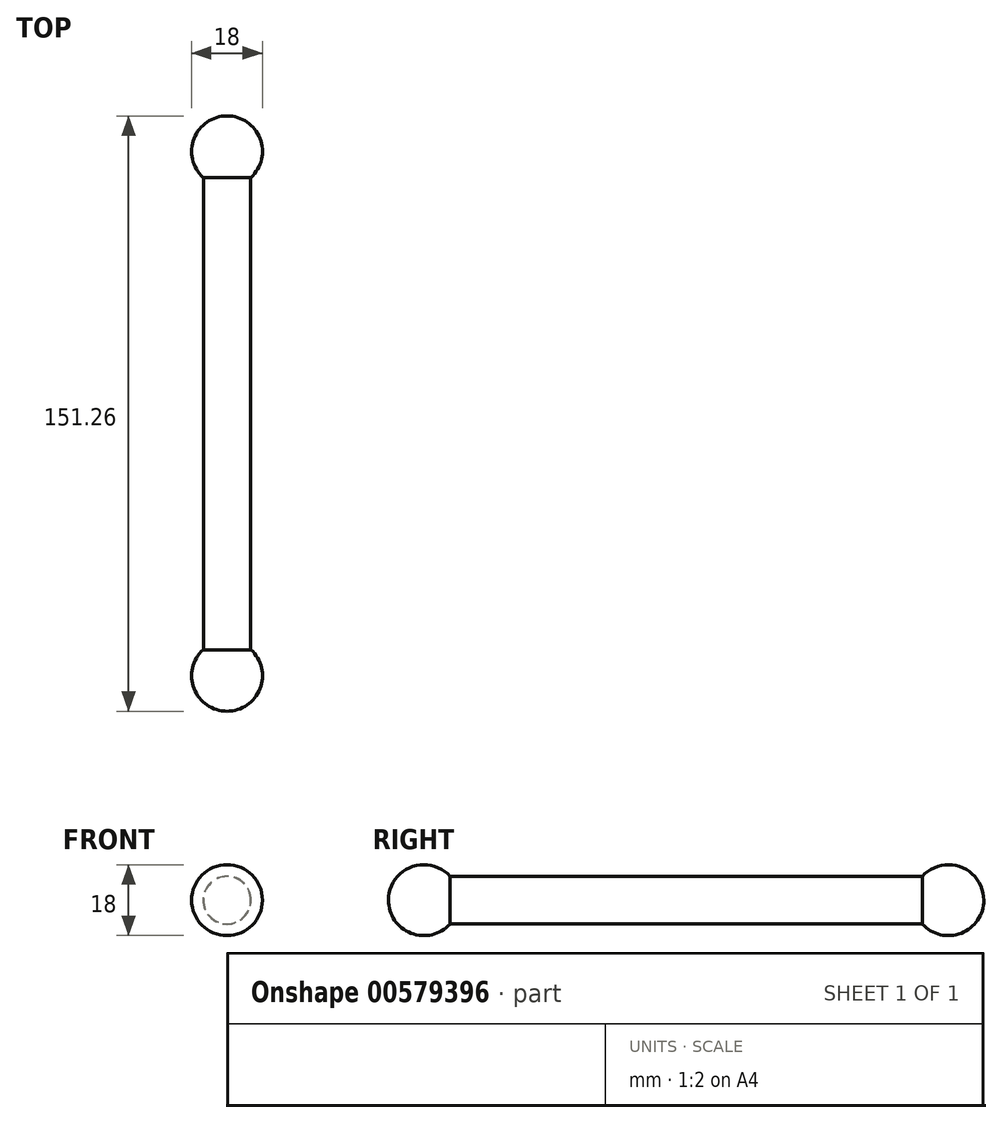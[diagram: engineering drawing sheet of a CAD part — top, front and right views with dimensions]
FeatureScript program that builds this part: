
annotation { "Feature Type Name" : "Feature", "Feature Type Description" : "" }
export const myFeature = defineFeature(function(context is Context, id is Id, definition is map)
    precondition{}
    {
        {
            var Q0;
            Q0=qCreatedBy(makeId("Front.planeOp"),FACE);
            var sketch = newSketch(context, id + "F0", { "sketchPlane" : qUnion([Q0])});
            skCircle(sketch, "E0", {"center": v(0, 0) * mm, "radius": 6 * mm});
            skSolve(sketch);
        }
        {
            var Q0;
            Q0 = qSketchRegion(id + "F0", true);
            extrude(context, id + "F1", {"entities" : qUnion([Q0]), "endBound" : BoundingType.SYMMETRIC, "depth" : 120 * mm, "offsetDistance" : 25 * mm});
        }
        {
            var Q0;
            Q0=qCreatedBy(makeId("Right.planeOp"),FACE);
            var sketch = newSketch(context, id + "F2", { "sketchPlane" : qUnion([Q0])});
            skLineSegment(sketch, "E1", {"start": v(-60, 0) * mm, "end": v(-87.62, 0) * mm, "construction": true});
            skArc(sketch, "E2", {"start": v(-60, 6.1) * mm, "mid": v(-69.9, 8.39) * mm, "end": v(-75.63, 0) * mm});
            skPoint(sketch, "E3", {"position": v(-60, 6.1) * mm});
            skLineSegment(sketch, "E4", {"start": v(-60, 0) * mm, "end": v(-60, 6.1) * mm});
            skLineSegment(sketch, "E5", {"start": v(-60, 0) * mm, "end": v(-75.63, 0) * mm});
            skSolve(sketch);
        }
        {
            var Q0;
            Q0 = qSketchRegion(id + "F2", true);
            var Q1;
            Q1=sQuery(id+"F2.wireOp",EDGE,"E1");
            revolve(context, id + "F3", {"operationType" : NewBodyOperationType.ADD, "entities" : qUnion([Q0]), "axis" : qUnion([Q1]), "revolveType" : RevolveType.FULL});
        }
        {
            var Q0;
            Q0=makeQuery(id+"F1.opExtrude","SWEPT_BODY",BODY,{"disambiguationData":[OSD([sQuery(id+"F0.wireOp",EDGE,"E0")])]});
            var Q1;
            Q1=qCreatedBy(makeId("Front.planeOp"),FACE);
            mirror(context, id + "F4", {"entities" : qUnion([Q0]), "mirrorPlane" : qUnion([Q1])});
        }
    });
